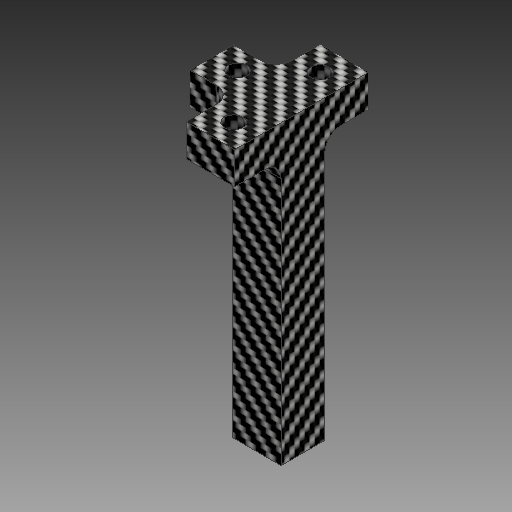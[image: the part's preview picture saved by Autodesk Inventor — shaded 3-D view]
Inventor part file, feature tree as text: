
AUTODESK INVENTOR PART (.ipt)
format: ipt  version: 2018 (Build 220112000, 112)  size: 243,712 bytes
history: native  units: mm
features: sketch x5, other x3
ambient origin geometry x8: Origin, YZ Plane, XZ Plane, XY Plane, X Axis, Y Axis, Z Axis, Center Point
bodies: Volumenkörper1 (feature_tree)
feature tree (8):
  other  "SolarpanelHalterung1.ipt"
  other  "Volumenkörper1::SolarpanelHalterung1.ipt"
  other  "Bezeichnung1"
  sketch  "Skizze1"  dims[d0=10.0mm]
  sketch  "Skizze2"
  sketch  "Skizze3"
  sketch  "Skizze4"
  sketch  "Skizze5"
